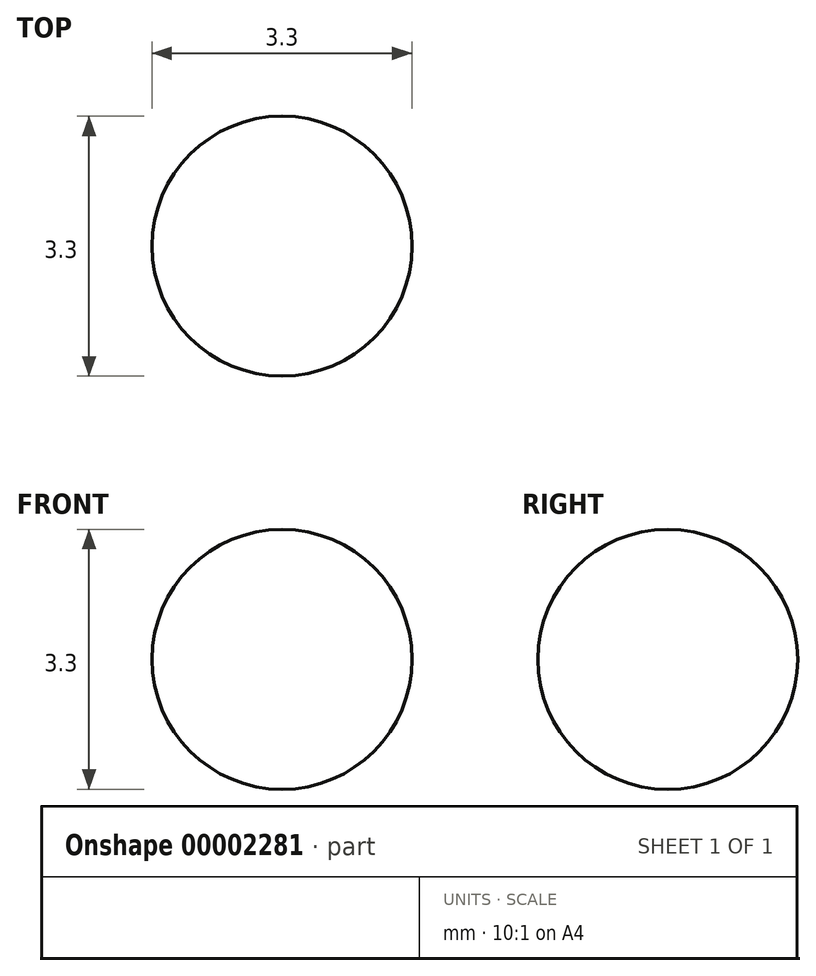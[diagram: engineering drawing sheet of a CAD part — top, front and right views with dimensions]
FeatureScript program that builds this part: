
annotation { "Feature Type Name" : "Feature", "Feature Type Description" : "" }
export const myFeature = defineFeature(function(context is Context, id is Id, definition is map)
    precondition{}
    {
        {
            var Q0;
            Q0=qCreatedBy(makeId("Top.planeOp"),FACE);
            var sketch = newSketch(context, id + "F0", { "sketchPlane" : qUnion([Q0])});
            skArc(sketch, "E0", {"start": v(0, 1.65) * mm, "mid": v(-1.65, 0) * mm, "end": v(0, -1.65) * mm});
            skLineSegment(sketch, "E1", {"start": v(0, -2.23) * mm, "end": v(0, 2.17) * mm, "construction": true});
            skLineSegment(sketch, "E2", {"start": v(0, -1.65) * mm, "end": v(0, 1.65) * mm});
            skSolve(sketch);
        }
        {
            var Q0;
            Q0=makeQuery(id+"F0.imprint","IMPRINT",FACE,{"disambiguationData":[TD([[makeQuery(id+"F0.imprint","IMPRINT",EDGE,{"derivedFrom":sQuery(id+"F0.wireOp",EDGE,"E0")}),1.0]])]});
            var Q1;
            Q1=sQuery(id+"F0.wireOp",EDGE,"E1");
            revolve(context, id + "F1", {"entities" : qUnion([Q0]), "axis" : qUnion([Q1]), "revolveType" : RevolveType.FULL});
        }
    });
